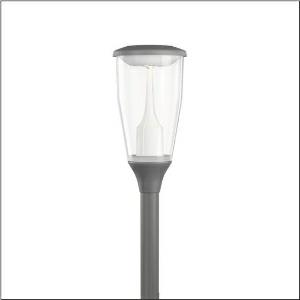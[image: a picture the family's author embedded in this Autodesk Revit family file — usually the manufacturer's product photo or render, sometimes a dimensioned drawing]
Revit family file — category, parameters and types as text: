
# Revit family: dl_11_iq___st1_2a_5xa5565mf14h000022_0c06
name_source: partatom
category: Lighting Fixtures
units: mm (PartAtom-declared; Revit-internal decimal feet)

## family parameters
Cut with Voids When Loaded = No
Host = Face
Light Source = No
Part Type = Normal
Room Calculation Point = No
Round Connector Dimension = Use Diameter
Shared = No

## types (1)
- --- (1 x LED, 1560 lm, 11.8 W, 2700K)
    Apparent Load = 12 VA
    CIE Flux Codes = 24 63 94 96 100
    Color Rendering = 70
    Color Temperature = 2700K
    Default Elevation = 1800 mm
    Description = DL 11 iQ, mast luminaire, Module 540 iQ-SR, primary light control with 3 zone facetted reflector, of plastic, silver coated, highly specular, structured, primary optical cover: cover, of PMMA, transparent, light distribution: ST1.2a, light emission: direct distribution, primary light characteristic: asymmetric, installation type: post-top, LED, High Power LED, rated luminous flux: 1.560lm, luminous efficacy: 149lm/W, light colour: 727, colour temperature: 2700K, control gear: iQ Street-Remote, control: Street-Remote, Auto-Match, Temp-Guard, Lumen-Switch, Night-Set, Smart-Wire, Light-Fading, Desk-Remote (wireless, voltage-free reading and setting of iQ features in the workshop via application-optimized NFC function/RFID function), optimised constant luminous flux control (CLO 2.0), mains connection: 220..240V, AC, 50/60Hz, connection cable pre-assembled, cable length: 5,5m, start of lifetime: 12W, end of service life: 12W, reduction: 5W, luminaire housing, upper part, of diecast aluminium, coated, Siteco® metallic grey (DB 702S), spigot size: 60mm (post-top), mounting height: 3..5m, post-top mast mounting element, of diecast aluminium, coated, Siteco® metallic grey (DB 702S), Module 540 iQ-SR, traffic white (RAL 9016), equipment: standard, protection rating (complete): IP66, insulation class (complete): insulation class II (safety insulation), certification: CE, ENEC, ENEC+, VDE, impact resistance: IK07, packaging unit: 1 piece

Light Distribution: ST1.2a
    Height = 665 mm
    Lamp = 1 x LED
    Lamp Light Flux = 1560 lm
    Lamp Power = 11.8 W
    Lamp count = 1
    Length = 334 mm
    Luminous efficacy = 132 lm/W
    Manufacturer = Siteco
    ModVariant = No
    Model = 5XA5565MF14H000022
    Number of Poles = 1
    OnlyDefault = Yes
    Power Factor = 1
    Product Name = DL 11 iQ | ST1.2a
    Product group = mast luminaire | pylon top
    ProductGroupID = 6100
    Protection Class = Protection class II
    Protection Degree = IP 66
    RLX_Detail_Level = 1
    RLX_Emergency_Light_Flux = 0 lm
    RLX_Emergency_Type = 0
    RLX_Emergency_Type_DB = No
    RlxData = <blob elided: 139149 chars, md5=4869aa38>
    Socket = socket
    Standby Power = 0 W
    System Light Flux = 1560 lm
    System Power = 12 W
    Type Comments = factory setting: luminous flux: 100 % | dim-lin: 254 | 472 mA
    Type Image = l_1258354.jpg
    URL = http://relux.com
    VarID = @adj_116699
    Voltage = 0 V
    Weight = 0.00 kg
    Width = 0 mm  [stored 0 ft]

note: [stored X ft] marks values corroborated as IEEE doubles in the binary element streams (Revit-internal decimal feet)

## geometry (parser evidence)
native form markers: Blend x4, Sweep x11
no freeform markers — native parametric forms only
